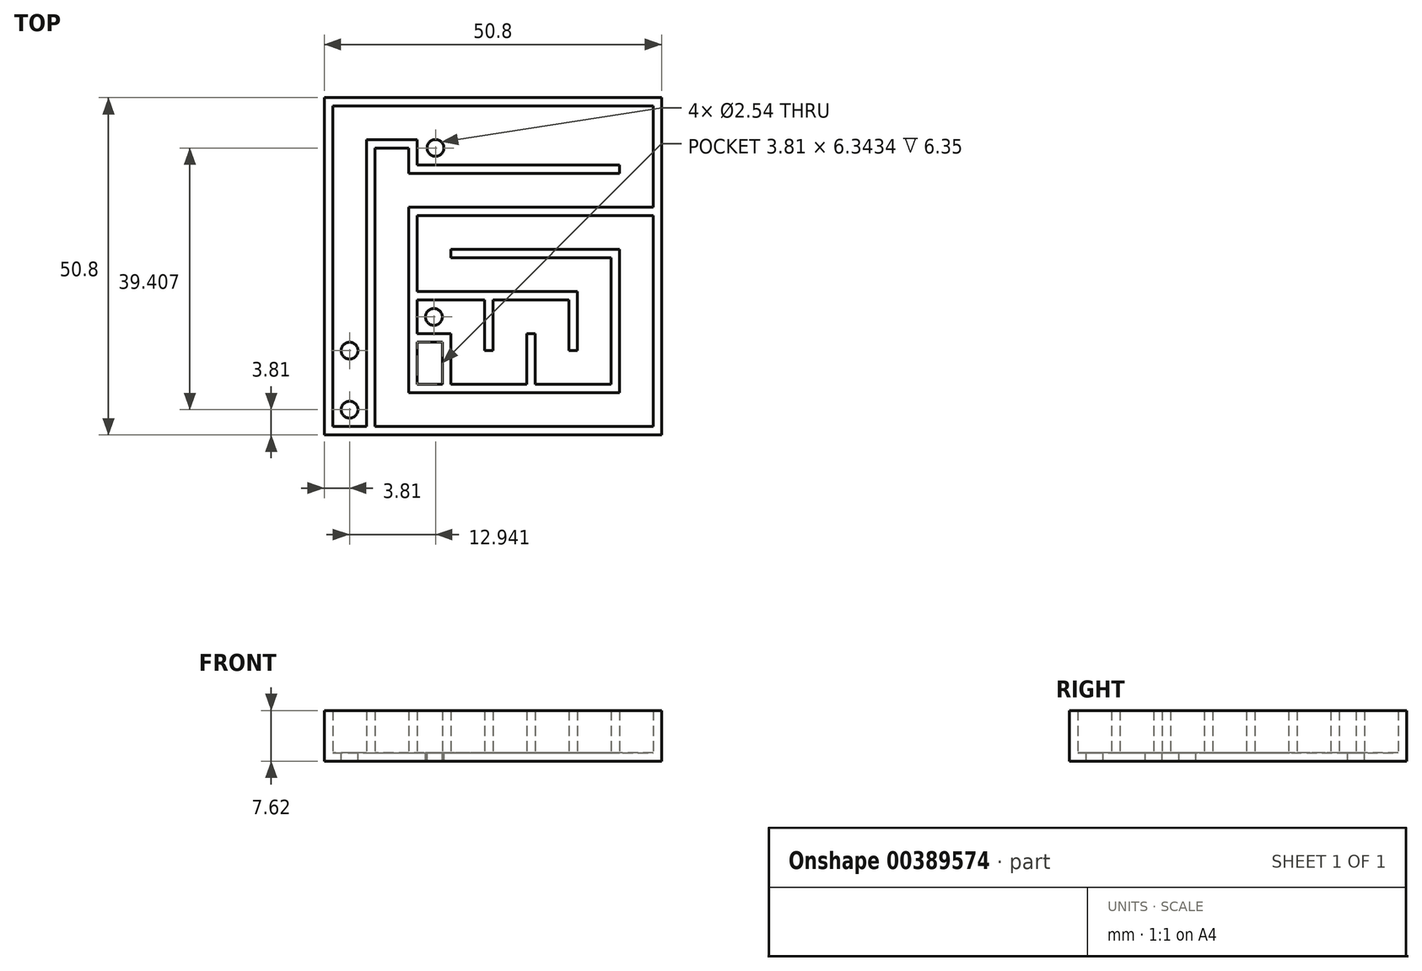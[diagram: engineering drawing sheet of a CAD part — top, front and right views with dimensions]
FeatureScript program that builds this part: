
annotation { "Feature Type Name" : "Feature", "Feature Type Description" : "" }
export const myFeature = defineFeature(function(context is Context, id is Id, definition is map)
    precondition{}
    {
        {
            var Q0;
            Q0=qCreatedBy(makeId("Top.planeOp"),FACE);
            var sketch = newSketch(context, id + "F0", { "sketchPlane" : qUnion([Q0])});
            skLineSegment(sketch, "E0", {"start": v(0, 0) * mm, "end": v(0, 50.8) * mm});
            skLineSegment(sketch, "E1", {"start": v(0, 50.8) * mm, "end": v(50.8, 50.8) * mm});
            skLineSegment(sketch, "E2", {"start": v(50.8, 50.8) * mm, "end": v(50.8, 0) * mm});
            skLineSegment(sketch, "E3", {"start": v(50.8, 0) * mm, "end": v(0, 0) * mm});
            skSolve(sketch);
        }
        {
            var Q0;
            Q0 = qSketchRegion(id + "F0", true);
            extrude(context, id + "F1", {"entities" : qUnion([Q0]), "depth" : 7.62 * mm});
        }
        {
            var Q0;
            Q0=makeQuery(id+"F1.opExtrude","CAP_FACE",FACE,{"disambiguationData":[OSD([sQuery(id+"F0.wireOp",EDGE,"E0"),sQuery(id+"F0.wireOp",EDGE,"E1"),sQuery(id+"F0.wireOp",EDGE,"E2"),sQuery(id+"F0.wireOp",EDGE,"E3")])],"isStart":false});
            shell(context, id + "F2", {"entities" : qUnion([Q0]), "thickness" : 1.27 * mm});
        }
        {
            var Q0;
            Q0=makeQuery(id+"F2.opShell","OFFSET_FACE",FACE,{"disambiguationData":[OSD([sQuery(id+"F0.wireOp",EDGE,"E0"),sQuery(id+"F0.wireOp",EDGE,"E1"),sQuery(id+"F0.wireOp",EDGE,"E2"),sQuery(id+"F0.wireOp",EDGE,"E3")])]});
            var sketch = newSketch(context, id + "F3", { "sketchPlane" : qUnion([Q0])});
            skLineSegment(sketch, "E4", {"start": v(6.35, 1.27) * mm, "end": v(6.35, 44.45) * mm});
            skLineSegment(sketch, "E5", {"start": v(6.35, 44.45) * mm, "end": v(7.62, 44.45) * mm});
            skLineSegment(sketch, "E6", {"start": v(7.62, 44.45) * mm, "end": v(7.62, 1.27) * mm});
            skLineSegment(sketch, "E7", {"start": v(7.62, 1.27) * mm, "end": v(6.35, 1.27) * mm});
            skSolve(sketch);
        }
        {
            var Q0;
            Q0=makeQuery(id+"F3.imprint","IMPRINT",FACE,{"disambiguationData":[TD([[makeQuery(id+"F3.imprint","IMPRINT",EDGE,{"derivedFrom":sQuery(id+"F3.wireOp",EDGE,"E4")}),-1.0]])]});
            extrude(context, id + "F4", {"entities" : qUnion([Q0]), "operationType" : NewBodyOperationType.ADD, "depth" : 6.35 * mm});
        }
        {
            var Q0;
            Q0=makeQuery(id+"F2.opShell","OFFSET_FACE",FACE,{"disambiguationData":[OSD([sQuery(id+"F0.wireOp",EDGE,"E0"),sQuery(id+"F0.wireOp",EDGE,"E1"),sQuery(id+"F0.wireOp",EDGE,"E2"),sQuery(id+"F0.wireOp",EDGE,"E3")])]});
            var sketch = newSketch(context, id + "F5", { "sketchPlane" : qUnion([Q0])});
            skCircle(sketch, "E8", {"center": v(3.81, 3.81) * mm, "radius": 1.27 * mm});
            skSolve(sketch);
        }
        {
            var Q0;
            Q0 = qSketchRegion(id + "F5", true);
            extrude(context, id + "F6", {"entities" : qUnion([Q0]), "operationType" : NewBodyOperationType.REMOVE, "oppositeDirection" : true, "depth" : 25.4 * mm});
        }
        {
            var Q0;
            Q0=makeQuery(id+"F2.opShell","OFFSET_FACE",FACE,{"disambiguationData":[OSD([sQuery(id+"F0.wireOp",EDGE,"E0"),sQuery(id+"F0.wireOp",EDGE,"E1"),sQuery(id+"F0.wireOp",EDGE,"E2"),sQuery(id+"F0.wireOp",EDGE,"E3")])]});
            var sketch = newSketch(context, id + "F7", { "sketchPlane" : qUnion([Q0])});
            skLineSegment(sketch, "E9", {"start": v(7.62, 44.45) * mm, "end": v(13.97, 44.45) * mm});
            skLineSegment(sketch, "E10", {"start": v(13.97, 44.45) * mm, "end": v(13.97, 40.63) * mm});
            skLineSegment(sketch, "E11", {"start": v(13.97, 40.63) * mm, "end": v(44.45, 40.63) * mm});
            skLineSegment(sketch, "E12", {"start": v(7.62, 43.18) * mm, "end": v(12.7, 43.18) * mm});
            skLineSegment(sketch, "E13", {"start": v(44.45, 40.63) * mm, "end": v(44.45, 39.36) * mm});
            skLineSegment(sketch, "E14", {"start": v(44.45, 39.36) * mm, "end": v(12.7, 39.36) * mm});
            skLineSegment(sketch, "E15", {"start": v(12.7, 43.18) * mm, "end": v(12.7, 39.36) * mm});
            skSolve(sketch);
        }
        {
            var Q0;
            {var subQ1=sQuery(id+"F7.wireOp",EDGE,"E9");Q0=makeQuery(id+"F7.imprint","IMPRINT",FACE,{"disambiguationData":[TD([[makeQuery(id+"F7.imprint","IMPRINT",EDGE,{"derivedFrom":subQ1}),-1.0]])]});}
            extrude(context, id + "F8", {"entities" : qUnion([Q0]), "operationType" : NewBodyOperationType.ADD, "depth" : 6.35 * mm});
        }
        {
            var Q0;
            Q0=makeQuery(id+"F2.opShell","OFFSET_FACE",FACE,{"disambiguationData":[OSD([sQuery(id+"F0.wireOp",EDGE,"E0"),sQuery(id+"F0.wireOp",EDGE,"E1"),sQuery(id+"F0.wireOp",EDGE,"E2"),sQuery(id+"F0.wireOp",EDGE,"E3")])]});
            var sketch = newSketch(context, id + "F9", { "sketchPlane" : qUnion([Q0])});
            skLineSegment(sketch, "E16", {"start": v(12.7, 34.28) * mm, "end": v(49.53, 34.28) * mm});
            skLineSegment(sketch, "E17", {"start": v(49.53, 34.28) * mm, "end": v(49.53, 33.01) * mm});
            skLineSegment(sketch, "E18", {"start": v(49.53, 33.01) * mm, "end": v(12.7, 33.01) * mm});
            skLineSegment(sketch, "E19", {"start": v(12.7, 33.01) * mm, "end": v(12.7, 34.28) * mm});
            skSolve(sketch);
        }
        {
            var Q0;
            Q0 = qSketchRegion(id + "F9", true);
            extrude(context, id + "F10", {"entities" : qUnion([Q0]), "operationType" : NewBodyOperationType.ADD, "depth" : 6.35 * mm});
        }
        {
            var Q0;
            Q0=makeQuery(id+"F2.opShell","OFFSET_FACE",FACE,{"disambiguationData":[OSD([sQuery(id+"F0.wireOp",EDGE,"E0"),sQuery(id+"F0.wireOp",EDGE,"E1"),sQuery(id+"F0.wireOp",EDGE,"E2"),sQuery(id+"F0.wireOp",EDGE,"E3")])]});
            var sketch = newSketch(context, id + "F11", { "sketchPlane" : qUnion([Q0])});
            skLineSegment(sketch, "E20", {"start": v(12.7, 33.01) * mm, "end": v(12.7, 6.35) * mm});
            skLineSegment(sketch, "E21", {"start": v(12.7, 6.35) * mm, "end": v(13.97, 6.35) * mm});
            skLineSegment(sketch, "E22", {"start": v(13.97, 6.35) * mm, "end": v(13.97, 33.01) * mm});
            skLineSegment(sketch, "E23", {"start": v(13.97, 33.01) * mm, "end": v(12.7, 33.01) * mm});
            skSolve(sketch);
        }
        {
            var Q0;
            Q0=makeQuery(id+"F11.imprint","IMPRINT",FACE,{"disambiguationData":[TD([[makeQuery(id+"F11.imprint","IMPRINT",EDGE,{"derivedFrom":sQuery(id+"F11.wireOp",EDGE,"E20")}),1.0]])]});
            extrude(context, id + "F12", {"entities" : qUnion([Q0]), "operationType" : NewBodyOperationType.ADD, "depth" : 6.35 * mm});
        }
        {
            var Q0;
            Q0=makeQuery(id+"F2.opShell","OFFSET_FACE",FACE,{"disambiguationData":[OSD([sQuery(id+"F0.wireOp",EDGE,"E0"),sQuery(id+"F0.wireOp",EDGE,"E1"),sQuery(id+"F0.wireOp",EDGE,"E2"),sQuery(id+"F0.wireOp",EDGE,"E3")])]});
            var sketch = newSketch(context, id + "F13", { "sketchPlane" : qUnion([Q0])});
            skLineSegment(sketch, "E24", {"start": v(13.97, 6.35) * mm, "end": v(44.45, 6.35) * mm});
            skLineSegment(sketch, "E25", {"start": v(44.45, 6.35) * mm, "end": v(44.45, 7.62) * mm});
            skLineSegment(sketch, "E26", {"start": v(44.45, 7.62) * mm, "end": v(13.97, 7.62) * mm});
            skLineSegment(sketch, "E27", {"start": v(13.97, 7.62) * mm, "end": v(13.97, 6.35) * mm});
            skSolve(sketch);
        }
        {
            var Q0;
            Q0 = qSketchRegion(id + "F13", true);
            extrude(context, id + "F14", {"entities" : qUnion([Q0]), "operationType" : NewBodyOperationType.ADD, "depth" : 6.35 * mm});
        }
        {
            var Q0;
            Q0=makeQuery(id+"F2.opShell","OFFSET_FACE",FACE,{"disambiguationData":[OSD([sQuery(id+"F0.wireOp",EDGE,"E0"),sQuery(id+"F0.wireOp",EDGE,"E1"),sQuery(id+"F0.wireOp",EDGE,"E2"),sQuery(id+"F0.wireOp",EDGE,"E3")])]});
            var sketch = newSketch(context, id + "F15", { "sketchPlane" : qUnion([Q0])});
            skLineSegment(sketch, "E28", {"start": v(44.45, 7.62) * mm, "end": v(44.45, 27.93) * mm});
            skLineSegment(sketch, "E29", {"start": v(44.45, 27.93) * mm, "end": v(43.18, 27.93) * mm});
            skLineSegment(sketch, "E30", {"start": v(43.18, 27.93) * mm, "end": v(43.18, 7.62) * mm});
            skLineSegment(sketch, "E31", {"start": v(43.18, 7.62) * mm, "end": v(44.45, 7.62) * mm});
            skSolve(sketch);
        }
        {
            var Q0;
            Q0 = qSketchRegion(id + "F15", true);
            extrude(context, id + "F16", {"entities" : qUnion([Q0]), "operationType" : NewBodyOperationType.ADD, "depth" : 6.35 * mm});
        }
        {
            var Q0;
            Q0=makeQuery(id+"F2.opShell","OFFSET_FACE",FACE,{"disambiguationData":[OSD([sQuery(id+"F0.wireOp",EDGE,"E0"),sQuery(id+"F0.wireOp",EDGE,"E1"),sQuery(id+"F0.wireOp",EDGE,"E2"),sQuery(id+"F0.wireOp",EDGE,"E3")])]});
            var sketch = newSketch(context, id + "F17", { "sketchPlane" : qUnion([Q0])});
            skLineSegment(sketch, "E32", {"start": v(43.18, 27.93) * mm, "end": v(19.05, 27.93) * mm});
            skLineSegment(sketch, "E33", {"start": v(19.05, 27.93) * mm, "end": v(19.05, 26.66) * mm});
            skLineSegment(sketch, "E34", {"start": v(19.05, 26.66) * mm, "end": v(43.18, 26.66) * mm});
            skLineSegment(sketch, "E35", {"start": v(43.18, 26.66) * mm, "end": v(43.18, 27.93) * mm});
            skSolve(sketch);
        }
        {
            var Q0;
            Q0 = qSketchRegion(id + "F17", true);
            extrude(context, id + "F18", {"entities" : qUnion([Q0]), "operationType" : NewBodyOperationType.ADD, "depth" : 6.35 * mm});
        }
        {
            var Q0;
            Q0=makeQuery(id+"F2.opShell","OFFSET_FACE",FACE,{"disambiguationData":[OSD([sQuery(id+"F0.wireOp",EDGE,"E0"),sQuery(id+"F0.wireOp",EDGE,"E1"),sQuery(id+"F0.wireOp",EDGE,"E2"),sQuery(id+"F0.wireOp",EDGE,"E3")])]});
            var sketch = newSketch(context, id + "F19", { "sketchPlane" : qUnion([Q0])});
            skLineSegment(sketch, "E36", {"start": v(13.97, 21.58) * mm, "end": v(38.1, 21.58) * mm});
            skLineSegment(sketch, "E37", {"start": v(38.1, 21.58) * mm, "end": v(38.1, 20.31) * mm});
            skLineSegment(sketch, "E38", {"start": v(38.1, 20.31) * mm, "end": v(13.97, 20.31) * mm});
            skLineSegment(sketch, "E39", {"start": v(13.97, 20.31) * mm, "end": v(13.97, 21.58) * mm});
            skSolve(sketch);
        }
        {
            var Q0;
            Q0=makeQuery(id+"F19.imprint","IMPRINT",FACE,{"disambiguationData":[TD([[makeQuery(id+"F19.imprint","IMPRINT",EDGE,{"derivedFrom":sQuery(id+"F19.wireOp",EDGE,"E36")}),-1.0]])]});
            extrude(context, id + "F20", {"entities" : qUnion([Q0]), "operationType" : NewBodyOperationType.ADD, "depth" : 6.35 * mm});
        }
        {
            var Q0;
            Q0=makeQuery(id+"F2.opShell","OFFSET_FACE",FACE,{"disambiguationData":[OSD([sQuery(id+"F0.wireOp",EDGE,"E0"),sQuery(id+"F0.wireOp",EDGE,"E1"),sQuery(id+"F0.wireOp",EDGE,"E2"),sQuery(id+"F0.wireOp",EDGE,"E3")])]});
            var sketch = newSketch(context, id + "F21", { "sketchPlane" : qUnion([Q0])});
            skLineSegment(sketch, "E40", {"start": v(38.1, 20.31) * mm, "end": v(38.1, 12.7) * mm});
            skLineSegment(sketch, "E41", {"start": v(38.1, 12.7) * mm, "end": v(36.83, 12.7) * mm});
            skLineSegment(sketch, "E42", {"start": v(36.83, 12.7) * mm, "end": v(36.83, 20.31) * mm});
            skLineSegment(sketch, "E43", {"start": v(36.83, 20.31) * mm, "end": v(38.1, 20.31) * mm});
            skSolve(sketch);
        }
        {
            var Q0;
            Q0 = qSketchRegion(id + "F21", true);
            extrude(context, id + "F22", {"entities" : qUnion([Q0]), "operationType" : NewBodyOperationType.ADD, "depth" : 6.35 * mm});
        }
        {
            var Q0;
            Q0=makeQuery(id+"F2.opShell","OFFSET_FACE",FACE,{"disambiguationData":[OSD([sQuery(id+"F0.wireOp",EDGE,"E0"),sQuery(id+"F0.wireOp",EDGE,"E1"),sQuery(id+"F0.wireOp",EDGE,"E2"),sQuery(id+"F0.wireOp",EDGE,"E3")])]});
            var sketch = newSketch(context, id + "F23", { "sketchPlane" : qUnion([Q0])});
            skLineSegment(sketch, "E44", {"start": v(31.75, 7.62) * mm, "end": v(31.75, 15.23) * mm});
            skLineSegment(sketch, "E45", {"start": v(31.75, 15.23) * mm, "end": v(30.48, 15.23) * mm});
            skLineSegment(sketch, "E46", {"start": v(30.48, 15.23) * mm, "end": v(30.48, 7.62) * mm});
            skLineSegment(sketch, "E47", {"start": v(30.48, 7.62) * mm, "end": v(31.75, 7.62) * mm});
            skSolve(sketch);
        }
        {
            var Q0;
            Q0 = qSketchRegion(id + "F23", true);
            extrude(context, id + "F24", {"entities" : qUnion([Q0]), "operationType" : NewBodyOperationType.ADD, "depth" : 6.35 * mm});
        }
        {
            var Q0;
            Q0=makeQuery(id+"F2.opShell","OFFSET_FACE",FACE,{"disambiguationData":[OSD([sQuery(id+"F0.wireOp",EDGE,"E0"),sQuery(id+"F0.wireOp",EDGE,"E1"),sQuery(id+"F0.wireOp",EDGE,"E2"),sQuery(id+"F0.wireOp",EDGE,"E3")])]});
            var sketch = newSketch(context, id + "F25", { "sketchPlane" : qUnion([Q0])});
            skLineSegment(sketch, "E48", {"start": v(25.4, 20.31) * mm, "end": v(25.4, 12.7) * mm});
            skLineSegment(sketch, "E49", {"start": v(25.4, 12.7) * mm, "end": v(24.13, 12.7) * mm});
            skLineSegment(sketch, "E50", {"start": v(24.13, 12.7) * mm, "end": v(24.13, 20.31) * mm});
            skLineSegment(sketch, "E51", {"start": v(24.13, 20.31) * mm, "end": v(25.4, 20.31) * mm});
            skSolve(sketch);
        }
        {
            var Q0;
            Q0 = qSketchRegion(id + "F25", true);
            extrude(context, id + "F26", {"entities" : qUnion([Q0]), "operationType" : NewBodyOperationType.ADD, "depth" : 6.35 * mm});
        }
        {
            var Q0;
            Q0=makeQuery(id+"F2.opShell","OFFSET_FACE",FACE,{"disambiguationData":[OSD([sQuery(id+"F0.wireOp",EDGE,"E0"),sQuery(id+"F0.wireOp",EDGE,"E1"),sQuery(id+"F0.wireOp",EDGE,"E2"),sQuery(id+"F0.wireOp",EDGE,"E3")])]});
            var sketch = newSketch(context, id + "F27", { "sketchPlane" : qUnion([Q0])});
            skLineSegment(sketch, "E52", {"start": v(19.05, 7.62) * mm, "end": v(19.05, 15.23) * mm});
            skLineSegment(sketch, "E53", {"start": v(19.05, 15.23) * mm, "end": v(17.78, 15.23) * mm});
            skLineSegment(sketch, "E54", {"start": v(17.78, 15.23) * mm, "end": v(17.78, 7.62) * mm});
            skLineSegment(sketch, "E55", {"start": v(17.78, 7.62) * mm, "end": v(19.05, 7.62) * mm});
            skLineSegment(sketch, "E56", {"start": v(17.78, 15.23) * mm, "end": v(13.97, 15.23) * mm});
            skLineSegment(sketch, "E57", {"start": v(13.97, 15.23) * mm, "end": v(13.97, 13.96) * mm});
            skLineSegment(sketch, "E58", {"start": v(13.97, 13.96) * mm, "end": v(17.78, 13.96) * mm});
            skLineSegment(sketch, "E59", {"start": v(17.78, 13.96) * mm, "end": v(17.78, 15.23) * mm});
            skSolve(sketch);
        }
        {
            var Q0;
            Q0 = qSketchRegion(id + "F27", true);
            extrude(context, id + "F28", {"entities" : qUnion([Q0]), "operationType" : NewBodyOperationType.ADD, "depth" : 6.35 * mm});
        }
        {
            var Q0;
            {var subQ0=sQuery(id+"F0.wireOp",EDGE,"E2");var subQ1=sQuery(id+"F0.wireOp",EDGE,"E0");var subQ2=sQuery(id+"F0.wireOp",EDGE,"E3");var subQ3=sQuery(id+"F0.wireOp",EDGE,"E1");Q0=makeQuery(id+"F28.boolean.opBoolean","SPLIT",FACE,{"disambiguationData":[TD([makeQuery(id+"F2.opShell","OFFSET_FACE",FACE,{"disambiguationData":[OSD([subQ1])]})])],"derivedFrom":makeQuery(id+"F2.opShell","OFFSET_FACE",FACE,{"disambiguationData":[OSD([subQ1,subQ3,subQ0,subQ2])]})});}
            var sketch = newSketch(context, id + "F29", { "sketchPlane" : qUnion([Q0])});
            skCircle(sketch, "E60", {"center": v(16.51, 17.77) * mm, "radius": 1.27 * mm});
            skSolve(sketch);
        }
        {
            var Q0;
            Q0 = qSketchRegion(id + "F29", true);
            extrude(context, id + "F30", {"entities" : qUnion([Q0]), "operationType" : NewBodyOperationType.REMOVE, "oppositeDirection" : true, "depth" : 25.4 * mm});
        }
        {
            var Q0;
            {var subQ0=sQuery(id+"F0.wireOp",EDGE,"E2");var subQ1=sQuery(id+"F0.wireOp",EDGE,"E0");var subQ2=sQuery(id+"F0.wireOp",EDGE,"E3");var subQ3=sQuery(id+"F0.wireOp",EDGE,"E1");Q0=makeQuery(id+"F28.boolean.opBoolean","SPLIT",FACE,{"disambiguationData":[TD([makeQuery(id+"F2.opShell","OFFSET_FACE",FACE,{"disambiguationData":[OSD([subQ1])]})])],"derivedFrom":makeQuery(id+"F2.opShell","OFFSET_FACE",FACE,{"disambiguationData":[OSD([subQ1,subQ3,subQ0,subQ2])]})});}
            var sketch = newSketch(context, id + "F31", { "sketchPlane" : qUnion([Q0])});
            skCircle(sketch, "E61", {"center": v(3.81, 12.7) * mm, "radius": 1.27 * mm});
            skSolve(sketch);
        }
        {
            var Q0;
            Q0 = qSketchRegion(id + "F31", true);
            extrude(context, id + "F32", {"entities" : qUnion([Q0]), "operationType" : NewBodyOperationType.REMOVE, "oppositeDirection" : true, "depth" : 25.4 * mm});
        }
        {
            var Q0;
            {var subQ0=sQuery(id+"F0.wireOp",EDGE,"E2");var subQ1=sQuery(id+"F0.wireOp",EDGE,"E0");var subQ2=sQuery(id+"F0.wireOp",EDGE,"E3");var subQ3=sQuery(id+"F0.wireOp",EDGE,"E1");Q0=makeQuery(id+"F28.boolean.opBoolean","SPLIT",FACE,{"disambiguationData":[TD([makeQuery(id+"F2.opShell","OFFSET_FACE",FACE,{"disambiguationData":[OSD([subQ1])]})])],"derivedFrom":makeQuery(id+"F2.opShell","OFFSET_FACE",FACE,{"disambiguationData":[OSD([subQ1,subQ3,subQ0,subQ2])]})});}
            var sketch = newSketch(context, id + "F33", { "sketchPlane" : qUnion([Q0])});
            skCircle(sketch, "E62", {"center": v(16.75, 43.22) * mm, "radius": 1.27 * mm});
            skSolve(sketch);
        }
        {
            var Q0;
            Q0 = qSketchRegion(id + "F33", true);
            extrude(context, id + "F34", {"entities" : qUnion([Q0]), "operationType" : NewBodyOperationType.REMOVE, "oppositeDirection" : true, "depth" : 25.4 * mm});
        }
    });
